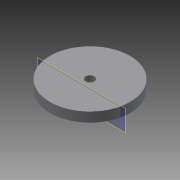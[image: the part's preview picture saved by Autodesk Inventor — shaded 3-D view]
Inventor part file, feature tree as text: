
AUTODESK INVENTOR PART (.ipt)
format: ipt  version: 2014 SP2 (Build 180246200, 246)  size: 100,864 bytes
history: native  units: mm
features: sketch x3, extrude x2, hole x2, plane x1, reference x1
ambient origin geometry x8: Origin, YZ Plane, XZ Plane, XY Plane, X Axis, Y Axis, Z Axis, Center Point
bodies: Solid1 (feature_tree)
feature tree (9):
  extrude  "Extrusion1"  Depth=11.0mm
  extrude  "Extrusion2"  Depth=10.0mm
  hole  "Hole1"  [1 undecoded]
  plane  "Work Plane1"
  hole  "Hole2"  [1 undecoded]
  sketch  "Sketch1"  dims[d0=6.0mm d1=0.0mm d2=11.0mm]
  reference  "Reference1"
  sketch  "Sketch2"  dims[d3=6.0mm d4=0.0mm d5=10.0mm d6=10.0mm]
  sketch  "Sketch3"  dims[d7=5.5mm d8=6.0mm d9=4.0mm d10=2.0mm d11=90.0deg d12=8.0mm d13=20.594885mm d14=3.0mm d15=3.5mm d16=6.0mm d17=4.0mm d18=2.0mm d19=90.0deg d20=8.0mm d21=20.594885mm]
note: 2 required parameter values undecoded (feature->parameter linkage not recoverable at this tier; creation-order binding heuristic only, values carry confidence <= 0.55)
